# Revit family: Screen
name_source: partatom
category: Windows
revit_build: Autodesk Revit 2017 (Build: 20190508_0315(x64)
units: mm (PartAtom-declared; Revit-internal decimal feet)

## family parameters
Always vertical = Yes
Cut with Voids When Loaded = No
Host = Wall
OmniClass Number = 23.30.20.00
OmniClass Title = Windows
Room Calculation Point = Yes
Shared = No

## types (4) — shared parameters
Default Sill Height = 800 mm  [stored 2.62467 ft]
Gebruikerstips = www.verozo.be/bim
Wall Closure = Neither

## per-type parameters (varying)
| type | Kast bovenop raam | Plansymboliek | Productiebreedte dagmaat | Productiehoogte dagmaat | Zijgeleiders op gevel |
| Voorbouw op raam - in dag | No | Yes | Yes | Yes | No |
| Voorbouw op gevel | No | Yes | No | No | Yes |
| Opbouw op raam | Yes | No | No | No | No |
| Voorbouw op raam - achter slag | No | No | No | No | No |

note: [stored X ft] marks values corroborated as IEEE doubles in the binary element streams (Revit-internal decimal feet)

## geometry (parser evidence)
native form markers: Sweep x2
no freeform markers — native parametric forms only
